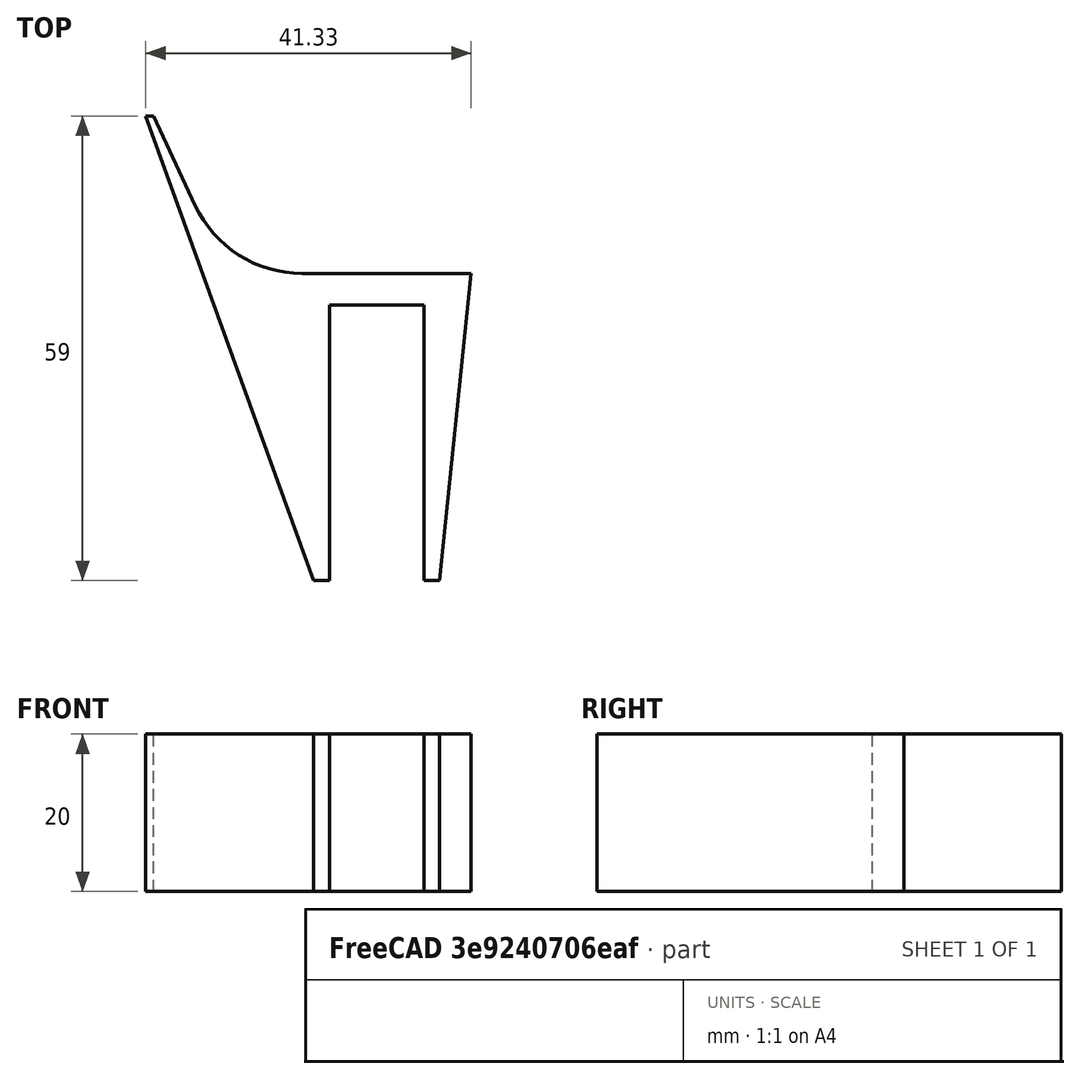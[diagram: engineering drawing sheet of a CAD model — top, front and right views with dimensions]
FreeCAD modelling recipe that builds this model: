
FCSTD DOCUMENT  (FreeCAD 2022.111R30764 (Git))
Label: cat bed bracket
License: All rights reserved
LicenseURL: http://en.wikipedia.org/wiki/All_rights_reserved
objects: Sketcher::SketchObject×1, PartDesign::Pad×1, PartDesign::Body×1
note: 5 computed .brp shape members not serialized (recipe doc carries the construction recipe); baked Part::Feature solids carry a one-line shape summary decoded from their .brp

FEATURE [Sketcher::SketchObject] Sketch
  FullyConstrained = true
  TreeRank = 11
  sketch-geometry (12):
    g0: LineSegment StartX=0 StartY=0 StartZ=0 EndX=0 EndY=-35 EndZ=0
    g1: LineSegment StartX=0 StartY=-35 StartZ=0 EndX=2 EndY=-35 EndZ=0
    g2: LineSegment StartX=2 StartY=-35 StartZ=0 EndX=6 EndY=4 EndZ=0
    g3: LineSegment StartX=6 StartY=4 StartZ=0 EndX=-15.4439 EndY=4 EndZ=0
    g4: LineSegment StartX=-29.0386 StartY=12.6607 StartZ=0 EndX=-34.3262 EndY=24 EndZ=0
    g5: LineSegment StartX=-34.3262 StartY=24 StartZ=0 EndX=-35.3262 EndY=24 EndZ=0
    g6: LineSegment StartX=-14 StartY=-35 StartZ=0 EndX=-12 EndY=-35 EndZ=0
    g7: LineSegment StartX=-12 StartY=-35 StartZ=0 EndX=-12 EndY=0 EndZ=0
    g8: LineSegment StartX=-12 StartY=0 StartZ=0 EndX=0 EndY=0 EndZ=0
    g9: ArcOfCircle CenterX=-15.4439 CenterY=19 CenterZ=0 NormalX=0 NormalY=0 NormalZ=1 AngleXU=0 Radius=15 StartAngle=3.57792 EndAngle=4.71239
    g10: GeomPoint [constr] X=-25 Y=4 Z=0
    g11: LineSegment StartX=-14 StartY=-35 StartZ=0 EndX=-35.3262 EndY=24 EndZ=0
  constraints (33):
    c: Coincident(g-1,g0)
    c: PointOnObject(g0,g-2)
    c: Coincident(g0,g1)
    c: Horizontal(g1)
    c: Coincident(g1,g2)
    c: Coincident(g2,g3)
    c: Horizontal(g3)
    c: Coincident(g4,g5)
    c: Horizontal(g5)
    c: Horizontal(g6)
    c: Coincident(g6,g7)
    c: PointOnObject(g7,g-1)
    c: Coincident(g7,g8)
    c: Coincident(g8,g0)
    c: Horizontal(g6,g0)
    c: DistanceY(g0,g0) = 35
    c: DistanceX(g1,g1) = 2
    c: DistanceX(g6,g6) = 2
    c: DistanceX(g6,g0) = 12
    c: DistanceY(g0,g2) = 4
    c: Vertical(g7)
    c: DistanceX(g0,g2) = 6
    c: DistanceX(g10,g7) = 13
    c: PointOnObject(g10,g3)
    c: PointOnObject(g10,g4)
    c: Tangent(g3,g9) = 1.5708
    c: Tangent(g4,g9) = 1.5708
    c: Diameter(g9) = 30
    c: DistanceX(g5,g5) = 1
    c: Angle(g3,g4) = 2.00713
    c: DistanceY(g3,g4) = 20
    c: Coincident(g11,g6)
    c: Coincident(g5,g11)
FEATURE [PartDesign::Pad] Pad
  AddSubType = 0
  AlongSketchNormal = false
  CheckUpToFaceLimits = true
  ClaimChildren = false
  Direction = (0,0,1)
  Fit = 0
  FitJoin = 0
  InnerFit = 0
  InnerFitJoin = 0
  InnerTaperAngle = 0
  InnerTaperAngleRev = 0
  Length = 20
  Length2 = 100
  Linearize = true
  NewSolid = false
  Profile = -> Sketch
  Suppress = false
  TreeRank = 12
  Type = 0
  _ProfileBasedVersion = 1
FEATURE [PartDesign::Body] Body
  AutoGroupSolids = false
  ExportMode = 0
  Group = -> [Sketch,Pad]
  Origin = -> Origin
  Tip = -> Pad
  TreeRank = 10
  _ExportChildren = -> [Pad]
  _GroupVersion = 1
